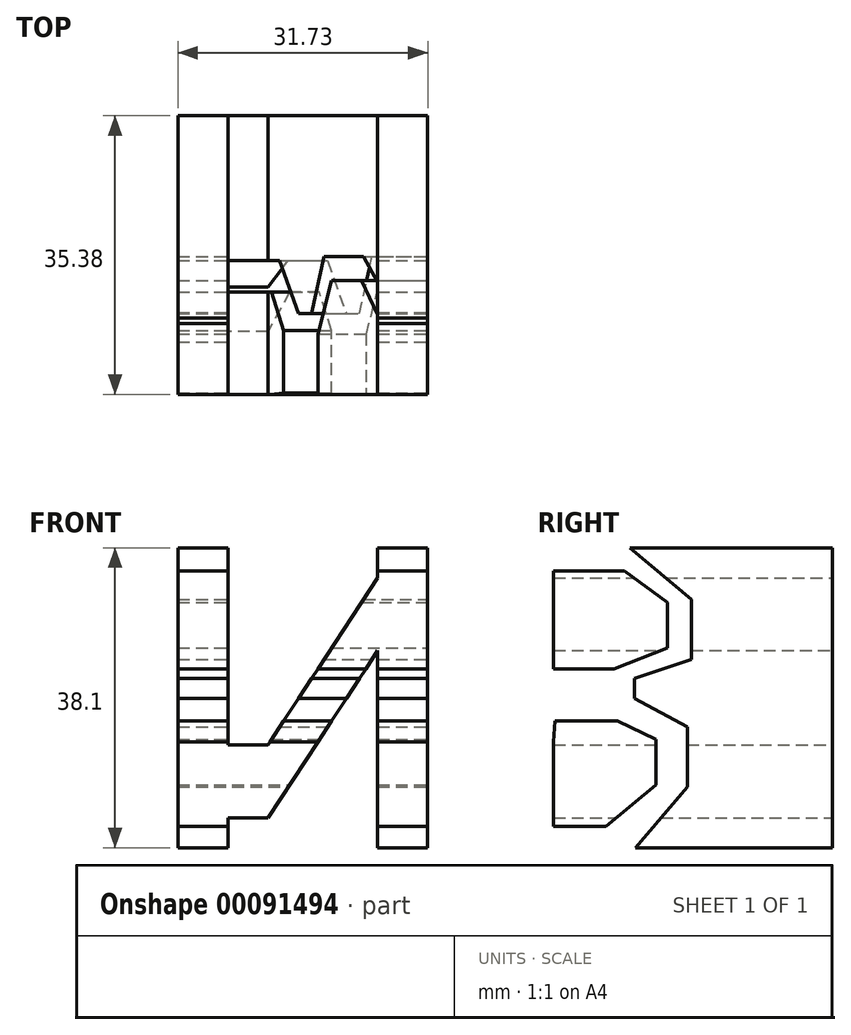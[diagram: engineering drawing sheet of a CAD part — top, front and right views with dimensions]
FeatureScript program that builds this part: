
annotation { "Feature Type Name" : "Feature", "Feature Type Description" : "" }
export const myFeature = defineFeature(function(context is Context, id is Id, definition is map)
    precondition{}
    {
        {
            var Q0;
            Q0=qCreatedBy(makeId("Front.planeOp"),FACE);
            var sketch = newSketch(context, id + "F0", { "sketchPlane" : qUnion([Q0])});
            skLineSegment(sketch, "E0", {"start": v(0, 0) * mm, "end": v(38.1, 0) * mm});
            skLineSegment(sketch, "E1", {"start": v(38.1, 0) * mm, "end": v(38.1, 38.1) * mm});
            skLineSegment(sketch, "E2", {"start": v(38.1, 38.1) * mm, "end": v(0, 38.1) * mm});
            skLineSegment(sketch, "E3", {"start": v(0, 38.1) * mm, "end": v(0, 0) * mm});
            skSolve(sketch);
        }
        {
            var Q0;
            Q0 = qSketchRegion(id + "F0", true);
            extrude(context, id + "F1", {"entities" : qUnion([Q0]), "depth" : 38.1 * mm});
        }
        {
            var Q0;
            Q0=qCreatedBy(makeId("Right.planeOp"),FACE);
            cPlane(context, id + "F2", {"entities" : qUnion([Q0]), "cplaneType" : CPlaneType.OFFSET, "offset" : 38.1 * mm, "width" : 152.4 * mm, "height" : 152.4 * mm});
        }
        {
            var Q0;
            Q0=qCreatedBy(id+"F2.planeOp",FACE);
            var sketch = newSketch(context, id + "F3", { "sketchPlane" : qUnion([Q0])});
            skLineSegment(sketch, "E4", {"start": v(-38.1, 38.1) * mm, "end": v(0, 38.1) * mm});
            skLineSegment(sketch, "E5", {"start": v(0, 38.1) * mm, "end": v(0, 0) * mm});
            skLineSegment(sketch, "E6", {"start": v(0, 0) * mm, "end": v(-38.42, 0) * mm});
            skLineSegment(sketch, "E7", {"start": v(-38.42, 0) * mm, "end": v(-38.1, 38.1) * mm});
            skLineSegment(sketch, "E8", {"start": v(-25.67, 38.1) * mm, "end": v(-17.9, 31.55) * mm});
            skLineSegment(sketch, "E9", {"start": v(-17.9, 31.55) * mm, "end": v(-17.9, 23.93) * mm});
            skLineSegment(sketch, "E10", {"start": v(-17.9, 23.93) * mm, "end": v(-25.12, 21.5) * mm});
            skLineSegment(sketch, "E11", {"start": v(-25.12, 21.5) * mm, "end": v(-25.12, 18.95) * mm});
            skLineSegment(sketch, "E12", {"start": v(-25.12, 18.95) * mm, "end": v(-18.4, 15.34) * mm});
            skLineSegment(sketch, "E13", {"start": v(-18.4, 15.34) * mm, "end": v(-18.4, 7.72) * mm});
            skLineSegment(sketch, "E14", {"start": v(-18.4, 7.72) * mm, "end": v(-25.02, 0) * mm});
            skLineSegment(sketch, "E15", {"start": v(-35.38, 35.13) * mm, "end": v(-35.38, 22.74) * mm});
            skLineSegment(sketch, "E16", {"start": v(-35.38, 22.74) * mm, "end": v(-27.71, 22.74) * mm});
            skLineSegment(sketch, "E17", {"start": v(-27.71, 22.74) * mm, "end": v(-20.93, 25.4) * mm});
            skLineSegment(sketch, "E18", {"start": v(-20.93, 25.4) * mm, "end": v(-20.93, 31.15) * mm});
            skLineSegment(sketch, "E19", {"start": v(-20.93, 31.15) * mm, "end": v(-26.38, 35.13) * mm});
            skLineSegment(sketch, "E20", {"start": v(-26.38, 35.13) * mm, "end": v(-35.38, 35.13) * mm});
            skLineSegment(sketch, "E21", {"start": v(-35.38, 13.45) * mm, "end": v(-35.38, 2.69) * mm});
            skLineSegment(sketch, "E22", {"start": v(-35.38, 2.69) * mm, "end": v(-28.74, 2.69) * mm});
            skLineSegment(sketch, "E23", {"start": v(-28.74, 2.69) * mm, "end": v(-22.4, 8) * mm});
            skLineSegment(sketch, "E24", {"start": v(-22.4, 8) * mm, "end": v(-22.4, 13.75) * mm});
            skLineSegment(sketch, "E25", {"start": v(-22.4, 13.75) * mm, "end": v(-27.27, 16.1) * mm});
            skLineSegment(sketch, "E26", {"start": v(-27.27, 16.1) * mm, "end": v(-35.23, 16.1) * mm});
            skLineSegment(sketch, "E27", {"start": v(-35.23, 16.1) * mm, "end": v(-35.38, 13.45) * mm});
            skSolve(sketch);
        }
        {
            var Q0;
            {var subQ1=sQuery(id+"F3.wireOp",EDGE,"E7");Q0=makeQuery(id+"F3.imprint","IMPRINT",FACE,{"disambiguationData":[TD([[makeQuery(id+"F3.imprint","IMPRINT",EDGE,{"derivedFrom":subQ1}),-1.0]])]});}
            extrude(context, id + "F4", {"entities" : qUnion([Q0]), "operationType" : NewBodyOperationType.REMOVE, "oppositeDirection" : true, "depth" : 38.1 * mm});
        }
        {
            var Q0;
            Q0=makeQuery(id+"F1.opExtrude","CAP_FACE",FACE,{"disambiguationData":[OSD([sQuery(id+"F0.wireOp",EDGE,"E0"),sQuery(id+"F0.wireOp",EDGE,"E1"),sQuery(id+"F0.wireOp",EDGE,"E2"),sQuery(id+"F0.wireOp",EDGE,"E3")])],"isStart":true});
            var sketch = newSketch(context, id + "F5", { "sketchPlane" : qUnion([Q0])});
            skLineSegment(sketch, "E28", {"start": v(-38.1, 38.1) * mm, "end": v(-38.1, 0) * mm});
            skLineSegment(sketch, "E29", {"start": v(-38.1, 0) * mm, "end": v(0, 0) * mm});
            skLineSegment(sketch, "E30", {"start": v(0, 0) * mm, "end": v(0, 38.1) * mm});
            skLineSegment(sketch, "E31", {"start": v(0, 38.1) * mm, "end": v(-38.1, 38.1) * mm});
            skLineSegment(sketch, "E32", {"start": v(-35.36, 38.1) * mm, "end": v(-35.36, 0) * mm});
            skLineSegment(sketch, "E33", {"start": v(-35.36, 0) * mm, "end": v(-29, 0) * mm});
            skLineSegment(sketch, "E34", {"start": v(-29, 0) * mm, "end": v(-29, 25.03) * mm});
            skLineSegment(sketch, "E35", {"start": v(-29, 25.03) * mm, "end": v(-15.06, 3.8) * mm});
            skLineSegment(sketch, "E36", {"start": v(-15.06, 3.81) * mm, "end": v(-9.98, 3.81) * mm});
            skLineSegment(sketch, "E37", {"start": v(-9.98, 3.81) * mm, "end": v(-9.98, 0) * mm});
            skLineSegment(sketch, "E38", {"start": v(-9.98, 0) * mm, "end": v(-3.63, 0) * mm});
            skLineSegment(sketch, "E39", {"start": v(-3.63, 0) * mm, "end": v(-3.63, 38.1) * mm});
            skLineSegment(sketch, "E40", {"start": v(-3.63, 38.1) * mm, "end": v(-9.98, 38.1) * mm});
            skLineSegment(sketch, "E41", {"start": v(-9.98, 38.1) * mm, "end": v(-9.98, 13.07) * mm});
            skLineSegment(sketch, "E42", {"start": v(-9.98, 13.07) * mm, "end": v(-15.06, 13.07) * mm});
            skLineSegment(sketch, "E43", {"start": v(-15.06, 13.07) * mm, "end": v(-29, 34.3) * mm});
            skLineSegment(sketch, "E44", {"start": v(-29, 34.3) * mm, "end": v(-29, 38.1) * mm});
            skSolve(sketch);
        }
        {
            var Q0;
            {var subQ0=sQuery(id+"F5.wireOp",EDGE,"E28");Q0=makeQuery(id+"F5.imprint","IMPRINT",FACE,{"disambiguationData":[TD([[makeQuery(id+"F5.imprint","IMPRINT",EDGE,{"derivedFrom":subQ0}),-1.0]])]});}
            var Q1;
            {var subQ0=sQuery(id+"F5.wireOp",EDGE,"E30");Q1=makeQuery(id+"F5.imprint","IMPRINT",FACE,{"disambiguationData":[TD([[makeQuery(id+"F5.imprint","IMPRINT",EDGE,{"derivedFrom":subQ0}),-1.0]])]});}
            var Q2;
            {var subQ0=sQuery(id+"F5.wireOp",EDGE,"E34");Q2=makeQuery(id+"F5.imprint","IMPRINT",FACE,{"disambiguationData":[TD([[makeQuery(id+"F5.imprint","IMPRINT",EDGE,{"derivedFrom":subQ0}),-1.0]])]});}
            var Q3;
            {var subQ0=sQuery(id+"F5.wireOp",EDGE,"E41");Q3=makeQuery(id+"F5.imprint","IMPRINT",FACE,{"disambiguationData":[TD([[makeQuery(id+"F5.imprint","IMPRINT",EDGE,{"derivedFrom":subQ0}),-1.0]])]});}
            extrude(context, id + "F6", {"entities" : qUnion([Q0, Q1, Q2, Q3]), "operationType" : NewBodyOperationType.REMOVE, "oppositeDirection" : true, "depth" : 38.1 * mm});
        }
    });
